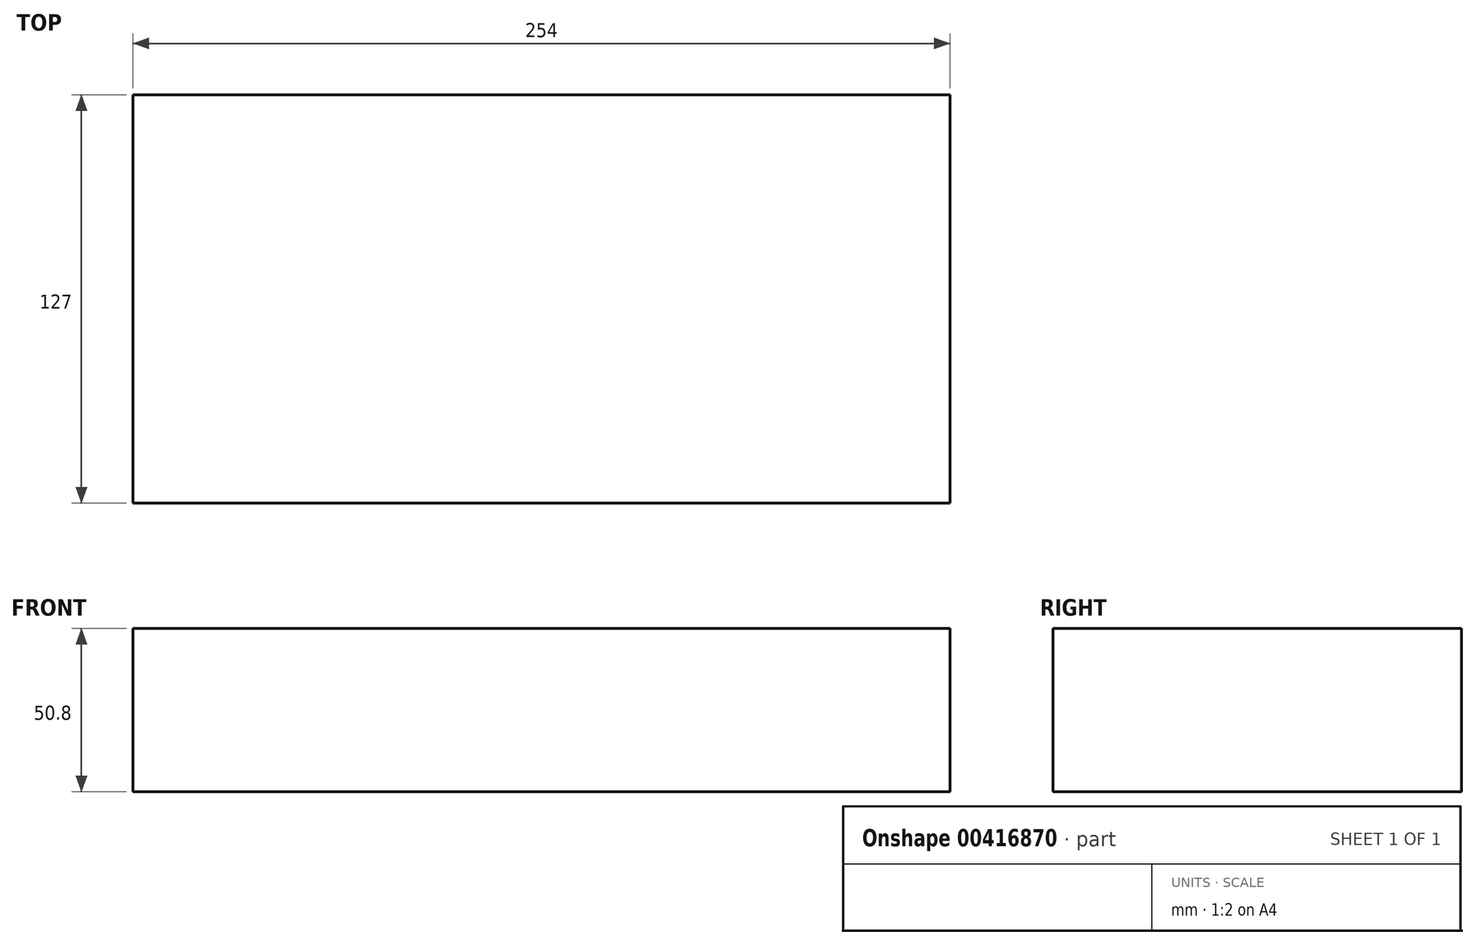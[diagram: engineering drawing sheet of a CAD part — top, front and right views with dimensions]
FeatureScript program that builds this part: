
annotation { "Feature Type Name" : "Feature", "Feature Type Description" : "" }
export const myFeature = defineFeature(function(context is Context, id is Id, definition is map)
    precondition{}
    {
        {
            var Q0;
            Q0=qCreatedBy(makeId("Top.planeOp"),FACE);
            var sketch = newSketch(context, id + "F0", { "sketchPlane" : qUnion([Q0])});
            skLineSegment(sketch, "E0.bottom", {"start": v(-127, 63.5) * mm, "end": v(127, 63.5) * mm});
            skLineSegment(sketch, "E0.top", {"start": v(-127, -63.5) * mm, "end": v(127, -63.5) * mm});
            skLineSegment(sketch, "E0.left", {"start": v(-127, 63.5) * mm, "end": v(-127, -63.5) * mm});
            skLineSegment(sketch, "E0.right", {"start": v(127, 63.5) * mm, "end": v(127, -63.5) * mm});
            skPoint(sketch, "E0.middle", {"position": v(0, 0) * mm});
            skSolve(sketch);
        }
        {
            var Q0;
            Q0 = qSketchRegion(id + "F0", true);
            extrude(context, id + "F1", {"entities" : qUnion([Q0]), "depth" : 50.8 * mm});
        }
    });
